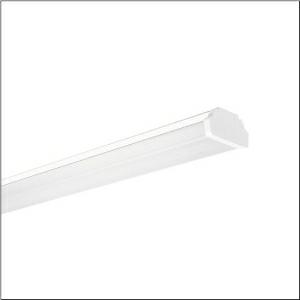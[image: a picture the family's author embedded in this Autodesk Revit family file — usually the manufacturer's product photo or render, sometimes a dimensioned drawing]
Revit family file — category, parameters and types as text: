
# Revit family: dus_r__31_ho_53bd812c1v6105_6b08
name_source: partatom
category: Lighting Fixtures
units: mm (PartAtom-declared; Revit-internal decimal feet)

## family parameters
Cut with Voids When Loaded = No
Host = Face
Light Source = No
Part Type = Normal
Room Calculation Point = No
Round Connector Dimension = Use Diameter
Shared = No

## types (1)
- --- (1 x LED, 10560 lm, 63.8 W, 6500K)
    Apparent Load = 64 VA
    CIE Flux Codes = 47 80 95 92 100
    Color Rendering = 80
    Color Temperature = 6500K
    Default Elevation = 1800 mm
    Description = DUS® 31 HOluminaire insert, length: 1.535mm, width: 81mm, height: 90mm, LED rated luminous flux: 10.560lm, light colour: 865, control gear: ON/OFF Multilumen, CLOi, control gear: ECG Multilumen, with plug, 3-pole, with phase selection, mains connection: 220..240V, AC, 50/60Hz, primary optical cover: cover, of PMMA, light emission: direct distribution, primary light characteristic: symmetric, protection rating (complete): IP20, protection rating (LED compartment): IP50, insulation class (complete): insulation class I (protective earthing), certification: CE, ENEC, VDE, UKCA, permissible ambient temperature for indoor applications: -35..+35°C, corresponds to IFS (International Featured Standards) requirements for safety and quality in the food industry, reducing of maximum allowable ambient temperature of 5°C with ceiling mounting, packaging unit: 1 piece
    Height = 95 mm
    Lamp = 1 x LED
    Lamp Light Flux = 10560 lm
    Lamp Power = 63.8 W
    Lamp count = 1
    Length = 1535 mm
    Luminous efficacy = 166 lm/W
    Manufacturer = Siteco
    ModVariant = No
    Model = 53BD812C1V6105
    Mounting Place = Ceiling
    Mounting Type = Pendant
    Number of Poles = 1
    OnlyDefault = Yes
    Power Factor = 1
    Product Name = DUS® 31 HO
    Product group = luminaire insert
    ProductGroupID = 902
    Protection Class = Protection class I
    Protection Degree = IP 20
    RLX_Detail_Level = 1
    RlxData = <blob elided: 39649 chars, md5=565037fd>
    Socket = socket
    Standby Power = 0 W
    System Light Flux = 10560 lm
    System Power = 64 W
    Type Comments = factory setting: luminous flux: 100 % | (A | C | E) | 144 mA
    Type Image = l_1003451.jpg
    URL = http://relux.com
    VarID = @adj_131253
    Voltage = 0 V
    Weight = 0.00 kg
    Width = 81 mm

## geometry (parser evidence)
native form markers: Blend x4, Sweep x12
no freeform markers — native parametric forms only
